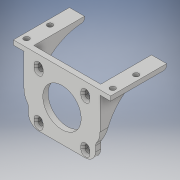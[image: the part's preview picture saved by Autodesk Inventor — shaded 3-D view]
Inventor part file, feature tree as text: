
AUTODESK INVENTOR PART (.ipt)
format: ipt  version: 2017 (Build 210142000, 142)  size: 291,328 bytes
history: native  units: in
note: dims shown in document units (in); Inventor stores cm internally (conversion verified against a paired STEP export)
features: extrude x7, sketch x7, reference x7, other x5, fillet x4, projected_geometry x2, chamfer x1
ambient origin geometry x8: Origin, YZ Plane, XZ Plane, XY Plane, X Axis, Y Axis, Z Axis, Center Point
bodies: Solid1 (feature_tree)
feature tree (33):
  extrude  "Extrusion1"  Depth=0.1378in
  extrude  "Extrusion3"  Depth=0.1181in TaperAngle=0.0deg
  extrude  "Extrusion4"  Depth=0.1181in TaperAngle=0.0deg
  extrude  "Extrusion5"  Depth=0.5in
  fillet  "Fillet1"  Radius=0.1181in
  fillet  "Fillet2"  Radius=0.1181in
  extrude  "Extrusion6"  Depth=0.1378in
  extrude  "Extrusion7"  Depth=0.0787in TaperAngle=0.0deg
  fillet  "Fillet3"  Radius=0.0787in
  fillet  "Fillet4"  Radius=0.0787in
  extrude  "Extrusion8"  Depth=0.0787in
  chamfer  "Chamfer1"  Distance=1.0in
  sketch  "Sketch1"  dims[d0=0.1378in d1=0.0in d4=0.0394in]
  reference  "Reference1"
  sketch  "Sketch3"  dims[d5=0.1181in d6=0.0in d7=0.1181in d8=0.0in]
  reference  "Reference2"
  sketch  "Sketch4"  dims[d9=0.1181in d10=0.2756in d11=0.0in]
  projected_geometry  "Projected Loop1"
  reference  "Reference3"
  sketch  "Sketch5"  dims[d12=0.125in d13=0.5in d14=0.1181in d15=0.1181in]
  sketch  "Sketch6"  dims[d16=0.2756in d17=0.0in d18=0.1378in]
  sketch  "Sketch7"  dims[d19=0.1378in d20=0.2756in d21=0.0in d22=0.0787in d23=0.0787in]
  reference  "Reference4"
  reference  "Reference5"
  sketch  "Sketch8"  dims[d24=1.0in d25=0.0787in d26=1.0in d27=0.0in d28=0.0591in d29=0.125in d30=45.0deg]
  projected_geometry  "Projected Loop2"
  reference  "Reference6"
  reference  "Reference7"
  other  "Rubiks Arm Assembly.iam"
  other  "Nema 17:1"
  other  "Base Plate:1"
  other  "Rubiks Cube Solver.iam"
  other  "bearing block:2"
